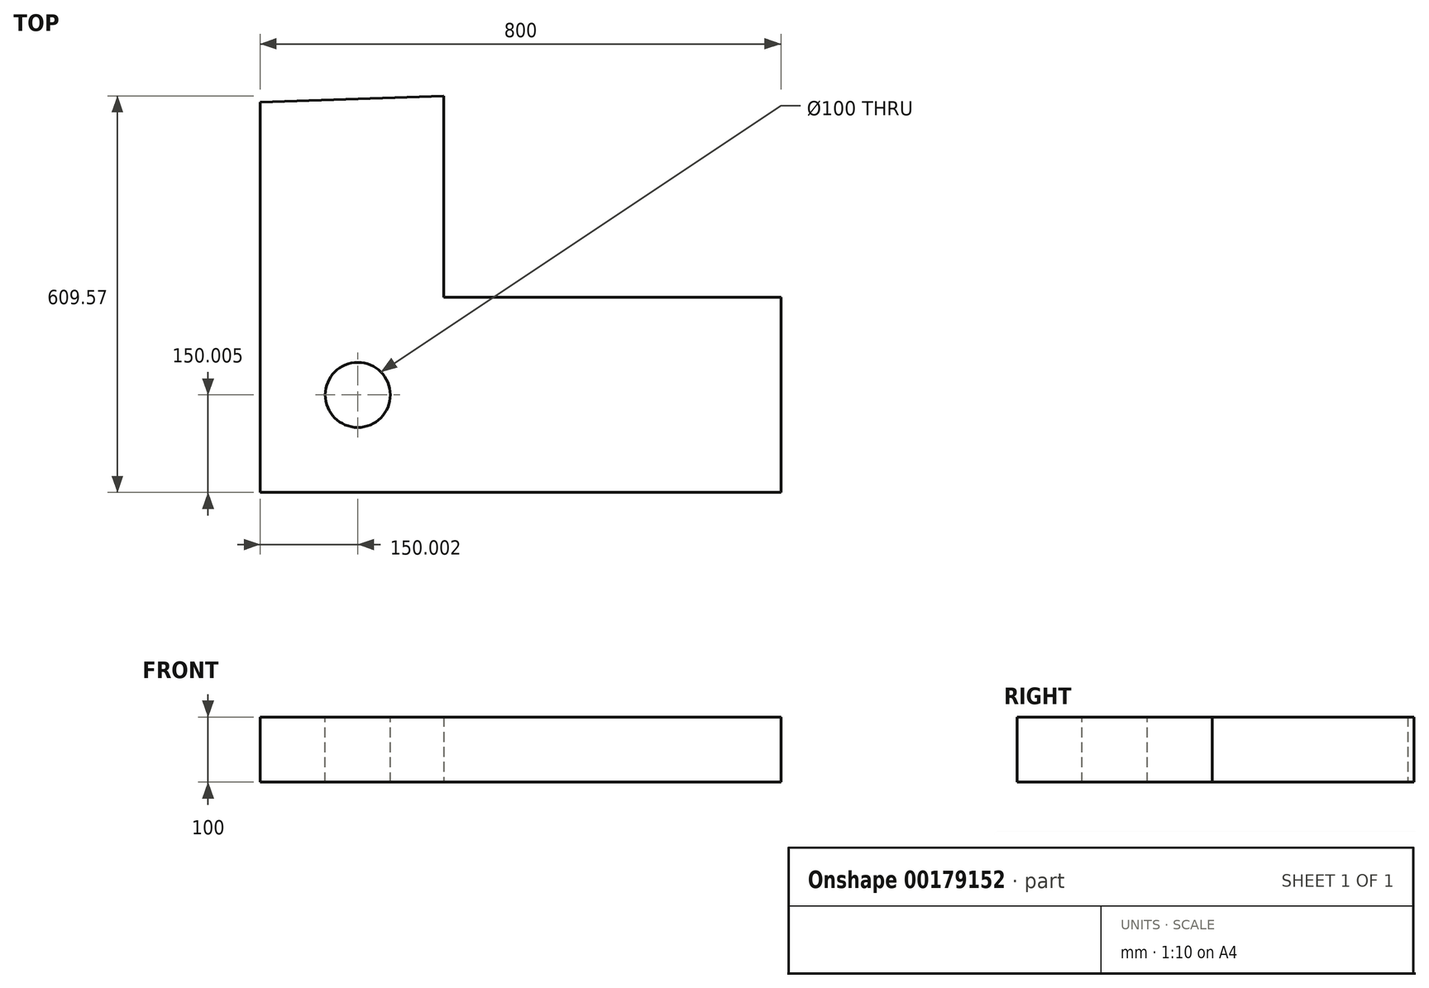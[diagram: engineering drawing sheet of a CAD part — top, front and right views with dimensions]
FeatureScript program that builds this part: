
annotation { "Feature Type Name" : "Feature", "Feature Type Description" : "" }
export const myFeature = defineFeature(function(context is Context, id is Id, definition is map)
    precondition{}
    {
        {
            var Q0;
            Q0=qCreatedBy(makeId("Top.planeOp"),FACE);
            var sketch = newSketch(context, id + "F0", { "sketchPlane" : qUnion([Q0])});
            skLineSegment(sketch, "E0", {"start": v(-386.25, 305.78) * mm, "end": v(-386.25, -294.22) * mm});
            skLineSegment(sketch, "E1", {"start": v(-386.25, -294.22) * mm, "end": v(413.75, -294.22) * mm});
            skLineSegment(sketch, "E2", {"start": v(413.75, -294.22) * mm, "end": v(413.75, 5.78) * mm});
            skLineSegment(sketch, "E3", {"start": v(413.75, 5.78) * mm, "end": v(-104.18, 5.78) * mm});
            skLineSegment(sketch, "E4", {"start": v(-104.18, 5.78) * mm, "end": v(-104.18, 315.35) * mm});
            skLineSegment(sketch, "E5", {"start": v(-104.18, 315.35) * mm, "end": v(-386.25, 305.78) * mm});
            skSolve(sketch);
        }
        {
            var Q0;
            Q0=makeQuery(id+"F0.imprint","IMPRINT",FACE,{"disambiguationData":[TD([[makeQuery(id+"F0.imprint","IMPRINT",EDGE,{"derivedFrom":sQuery(id+"F0.wireOp",EDGE,"E0")}),1.0]])]});
            extrude(context, id + "F1", {"entities" : qUnion([Q0]), "depth" : 100 * mm});
        }
        {
            var Q0;
            Q0=makeQuery(id+"F1.opExtrude","CAP_FACE",FACE,{"disambiguationData":[OSD([sQuery(id+"F0.wireOp",EDGE,"E0"),sQuery(id+"F0.wireOp",EDGE,"E1"),sQuery(id+"F0.wireOp",EDGE,"E2"),sQuery(id+"F0.wireOp",EDGE,"E3"),sQuery(id+"F0.wireOp",EDGE,"E4"),sQuery(id+"F0.wireOp",EDGE,"E5")])],"isStart":false});
            var sketch = newSketch(context, id + "F2", { "sketchPlane" : qUnion([Q0])});
            skLineSegment(sketch, "E6", {"start": v(-386.25, -294.22) * mm, "end": v(-386.25, -144.22) * mm, "construction": true});
            skLineSegment(sketch, "E7", {"start": v(-386.25, -144.22) * mm, "end": v(-236.25, -144.22) * mm, "construction": true});
            skLineSegment(sketch, "E8", {"start": v(-386.25, -294.22) * mm, "end": v(-236.25, -294.22) * mm, "construction": true});
            skLineSegment(sketch, "E9", {"start": v(-236.25, -294.22) * mm, "end": v(-236.25, -144.22) * mm, "construction": true});
            skCircle(sketch, "E10", {"center": v(-236.25, -144.22) * mm, "radius": 50 * mm});
            skSolve(sketch);
        }
        {
            var Q0;
            Q0=makeQuery(id+"F2.imprint","IMPRINT",FACE,{"disambiguationData":[TD([[makeQuery(id+"F2.imprint","IMPRINT",EDGE,{"derivedFrom":sQuery(id+"F2.wireOp",EDGE,"E10")}),1.0]])]});
            extrude(context, id + "F3", {"entities" : qUnion([Q0]), "operationType" : NewBodyOperationType.REMOVE, "oppositeDirection" : true, "depth" : 100 * mm});
        }
    });
